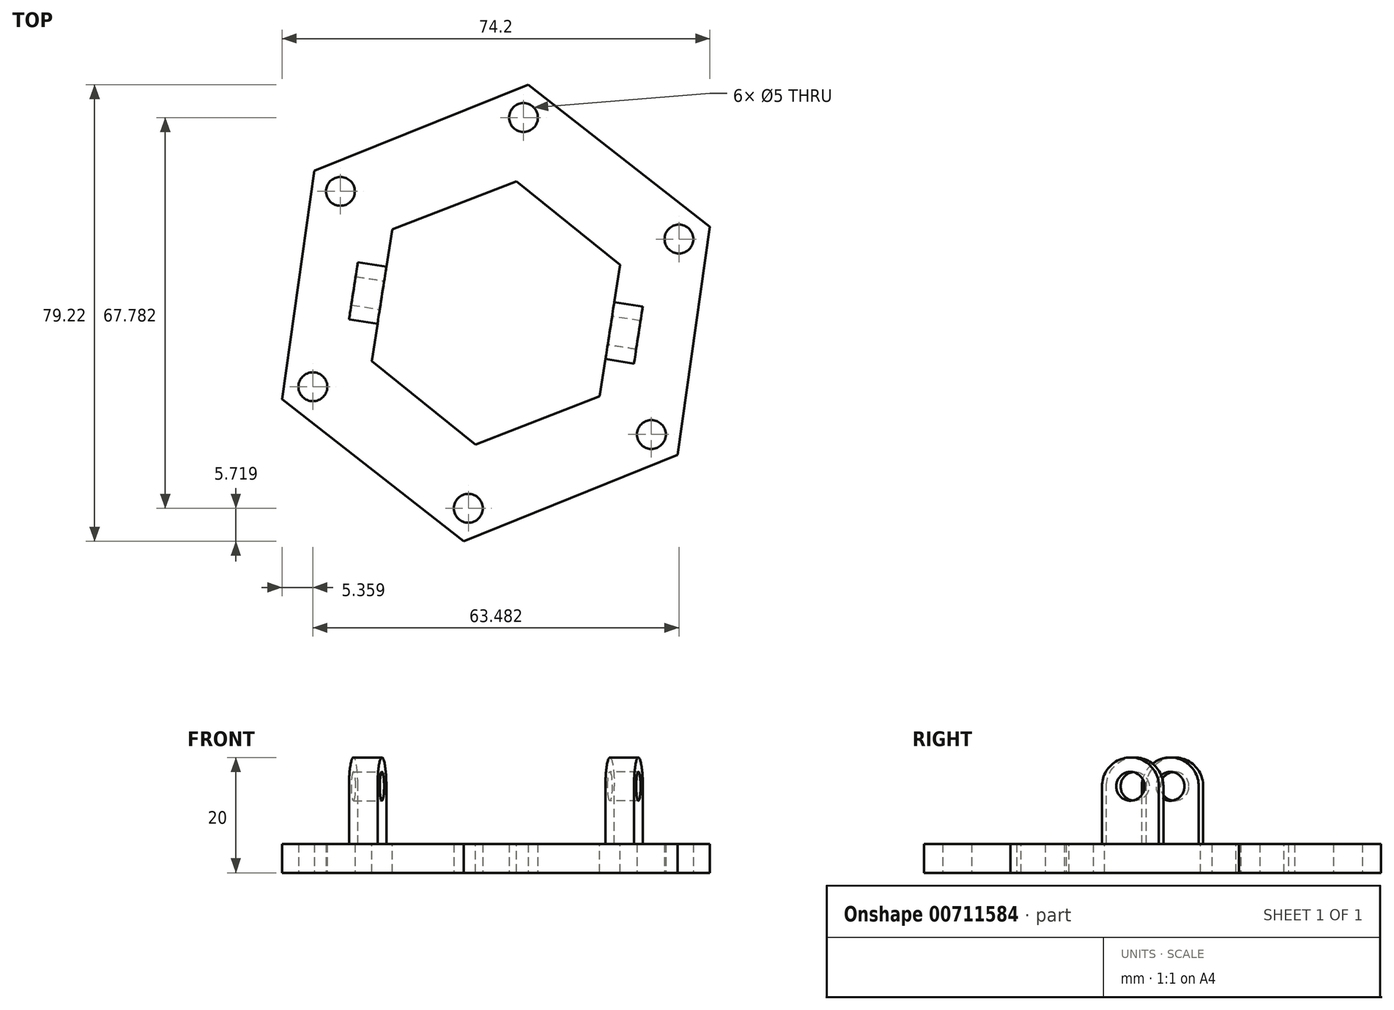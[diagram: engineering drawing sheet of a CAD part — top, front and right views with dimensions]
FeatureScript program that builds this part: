
annotation { "Feature Type Name" : "Feature", "Feature Type Description" : "" }
export const myFeature = defineFeature(function(context is Context, id is Id, definition is map)
    precondition{}
    {
        {
            var Q0;
            Q0=qCreatedBy(makeId("Top.planeOp"),FACE);
            var sketch = newSketch(context, id + "F0", { "sketchPlane" : qUnion([Q0])});
            skCircle(sketch, "E0.cCircle", {"center": v(0, 0) * mm, "radius": 34.64 * mm, "construction": true});
            skLineSegment(sketch, "E0.0", {"start": v(37.1, 14.96) * mm, "end": v(31.5, -24.64) * mm});
            skLineSegment(sketch, "E0.1", {"start": v(31.5, -24.64) * mm, "end": v(-5.59, -39.6) * mm});
            skLineSegment(sketch, "E0.2", {"start": v(-5.59, -39.6) * mm, "end": v(-37.1, -14.96) * mm});
            skLineSegment(sketch, "E0.3", {"start": v(-37.1, -14.96) * mm, "end": v(-31.5, 24.64) * mm});
            skLineSegment(sketch, "E0.4", {"start": v(-31.5, 24.64) * mm, "end": v(5.59, 39.6) * mm});
            skLineSegment(sketch, "E0.5", {"start": v(5.59, 39.6) * mm, "end": v(37.1, 14.96) * mm});
            skPoint(sketch, "E0.0.midPoint", {"position": v(34.3, -4.84) * mm});
            skSolve(sketch);
        }
        {
            var Q0;
            Q0=makeQuery(id+"F0.imprint","IMPRINT",FACE,{"disambiguationData":[TD([[makeQuery(id+"F0.imprint","IMPRINT",EDGE,{"derivedFrom":sQuery(id+"F0.wireOp",EDGE,"E0.0")}),-1.0]])]});
            extrude(context, id + "F1", {"entities" : qUnion([Q0]), "depth" : 5 * mm, "offsetDistance" : 25 * mm});
        }
        {
            var Q0;
            Q0=makeQuery(id+"F1.opExtrude","CAP_FACE",FACE,{"disambiguationData":[OSD([sQuery(id+"F0.wireOp",EDGE,"E0.0"),sQuery(id+"F0.wireOp",EDGE,"E0.1"),sQuery(id+"F0.wireOp",EDGE,"E0.2"),sQuery(id+"F0.wireOp",EDGE,"E0.3"),sQuery(id+"F0.wireOp",EDGE,"E0.4"),sQuery(id+"F0.wireOp",EDGE,"E0.5")])],"isStart":true});
            var sketch = newSketch(context, id + "F2", { "sketchPlane" : qUnion([Q0])});
            skCircle(sketch, "E1", {"center": v(26.96, 21.09) * mm, "radius": 2.5 * mm});
            skCircle(sketch, "E2", {"center": v(-4.78, 33.9) * mm, "radius": 2.5 * mm});
            skCircle(sketch, "E3", {"center": v(31.74, -12.8) * mm, "radius": 2.5 * mm});
            skCircle(sketch, "E4", {"center": v(4.78, -33.9) * mm, "radius": 2.5 * mm});
            skCircle(sketch, "E5", {"center": v(-26.96, -21.09) * mm, "radius": 2.5 * mm});
            skCircle(sketch, "E6", {"center": v(-31.74, 12.8) * mm, "radius": 2.5 * mm});
            skSolve(sketch);
        }
        {
            var Q0;
            Q0=makeQuery(id+"F2.imprint","IMPRINT",FACE,{"disambiguationData":[TD([[makeQuery(id+"F2.imprint","IMPRINT",EDGE,{"derivedFrom":sQuery(id+"F2.wireOp",EDGE,"E3")}),1.0]])]});
            var Q1;
            Q1=makeQuery(id+"F2.imprint","IMPRINT",FACE,{"disambiguationData":[TD([[makeQuery(id+"F2.imprint","IMPRINT",EDGE,{"derivedFrom":sQuery(id+"F2.wireOp",EDGE,"E4")}),1.0]])]});
            var Q2;
            Q2=makeQuery(id+"F2.imprint","IMPRINT",FACE,{"disambiguationData":[TD([[makeQuery(id+"F2.imprint","IMPRINT",EDGE,{"derivedFrom":sQuery(id+"F2.wireOp",EDGE,"E5")}),1.0]])]});
            var Q3;
            Q3=makeQuery(id+"F2.imprint","IMPRINT",FACE,{"disambiguationData":[TD([[makeQuery(id+"F2.imprint","IMPRINT",EDGE,{"derivedFrom":sQuery(id+"F2.wireOp",EDGE,"E6")}),1.0]])]});
            var Q4;
            Q4=makeQuery(id+"F2.imprint","IMPRINT",FACE,{"disambiguationData":[TD([[makeQuery(id+"F2.imprint","IMPRINT",EDGE,{"derivedFrom":sQuery(id+"F2.wireOp",EDGE,"E2")}),1.0]])]});
            var Q5;
            Q5=makeQuery(id+"F2.imprint","IMPRINT",FACE,{"disambiguationData":[TD([[makeQuery(id+"F2.imprint","IMPRINT",EDGE,{"derivedFrom":sQuery(id+"F2.wireOp",EDGE,"E1")}),1.0]])]});
            extrude(context, id + "F3", {"entities" : qUnion([Q0, Q1, Q2, Q3, Q4, Q5]), "operationType" : NewBodyOperationType.REMOVE, "oppositeDirection" : true, "depth" : 25 * mm, "offsetDistance" : 25 * mm});
        }
        {
            var Q0;
            Q0=makeQuery(id+"F1.opExtrude","CAP_FACE",FACE,{"disambiguationData":[OSD([sQuery(id+"F0.wireOp",EDGE,"E0.0"),sQuery(id+"F0.wireOp",EDGE,"E0.1"),sQuery(id+"F0.wireOp",EDGE,"E0.2"),sQuery(id+"F0.wireOp",EDGE,"E0.3"),sQuery(id+"F0.wireOp",EDGE,"E0.4"),sQuery(id+"F0.wireOp",EDGE,"E0.5")])],"isStart":false});
            var sketch = newSketch(context, id + "F4", { "sketchPlane" : qUnion([Q0])});
            skCircle(sketch, "E7.cCircle", {"center": v(0, 0) * mm, "radius": 20 * mm, "construction": true});
            skLineSegment(sketch, "E7.0", {"start": v(21.53, 8.34) * mm, "end": v(18, -14.48) * mm});
            skLineSegment(sketch, "E7.1", {"start": v(18, -14.48) * mm, "end": v(-3.54, -22.82) * mm});
            skLineSegment(sketch, "E7.2", {"start": v(-3.54, -22.82) * mm, "end": v(-21.53, -8.34) * mm});
            skLineSegment(sketch, "E7.3", {"start": v(-21.53, -8.34) * mm, "end": v(-18, 14.48) * mm});
            skLineSegment(sketch, "E7.4", {"start": v(-18, 14.48) * mm, "end": v(3.54, 22.82) * mm});
            skLineSegment(sketch, "E7.5", {"start": v(3.54, 22.82) * mm, "end": v(21.53, 8.34) * mm});
            skPoint(sketch, "E7.0.midPoint", {"position": v(19.76, -3.07) * mm});
            skSolve(sketch);
        }
        {
            var Q0;
            Q0=makeQuery(id+"F4.imprint","IMPRINT",FACE,{"disambiguationData":[TD([[makeQuery(id+"F4.imprint","IMPRINT",EDGE,{"derivedFrom":sQuery(id+"F4.wireOp",EDGE,"E7.0")}),-1.0]])]});
            extrude(context, id + "F5", {"entities" : qUnion([Q0]), "operationType" : NewBodyOperationType.REMOVE, "oppositeDirection" : true, "depth" : 6 * mm, "offsetDistance" : 25 * mm});
        }
        {
            var Q0;
            Q0=makeQuery(id+"F5.boolean.opBoolean","COPY",FACE,{"derivedFrom":makeQuery(id+"F5.opExtrude","SWEPT_FACE",FACE,{"disambiguationData":[OSD([sQuery(id+"F4.wireOp",EDGE,"E7.3")])]})});
            var sketch = newSketch(context, id + "F6", { "sketchPlane" : qUnion([Q0])});
            skLineSegment(sketch, "E8", {"start": v(-5, 5) * mm, "end": v(-5, 15) * mm});
            skLineSegment(sketch, "E9", {"start": v(5, 5) * mm, "end": v(5, 15) * mm});
            skArc(sketch, "E10", {"start": v(5, 15) * mm, "mid": v(0, 20) * mm, "end": v(-5, 15) * mm});
            skSolve(sketch);
        }
        {
            var Q0;
            {var subQ0=sQuery(id+"F6.wireOp",EDGE,"E8");Q0=makeQuery(id+"F6.imprint","IMPRINT",FACE,{"disambiguationData":[TD([[makeQuery(id+"F6.imprint","IMPRINT",EDGE,{"derivedFrom":subQ0}),-1.0]])]});}
            extrude(context, id + "F7", {"entities" : qUnion([Q0]), "operationType" : NewBodyOperationType.ADD, "oppositeDirection" : true, "depth" : 5 * mm, "offsetDistance" : 25 * mm});
        }
        {
            var Q0;
            {var subQ0=sQuery(id+"F4.wireOp",EDGE,"E7.3");Q0=makeQuery(id+"F7.boolean.opBoolean","MERGE",FACE,{"derivedFrom":[makeQuery(id+"F5.boolean.opBoolean","COPY",FACE,{"derivedFrom":makeQuery(id+"F5.opExtrude","SWEPT_FACE",FACE,{"disambiguationData":[OSD([subQ0])]})}),makeQuery(id+"F7.opExtrude","CAP_FACE",FACE,{"disambiguationData":[OSD([subQ0,sQuery(id+"F6.wireOp",EDGE,"E8"),sQuery(id+"F6.wireOp",EDGE,"E9"),sQuery(id+"F6.wireOp",EDGE,"E10")])],"isStart":true})]});}
            var sketch = newSketch(context, id + "F8", { "sketchPlane" : qUnion([Q0])});
            skCircle(sketch, "E11", {"center": v(0, 15) * mm, "radius": 2.5 * mm});
            skSolve(sketch);
        }
        {
            var Q0;
            Q0=makeQuery(id+"F8.imprint","IMPRINT",FACE,{"disambiguationData":[TD([[makeQuery(id+"F8.imprint","IMPRINT",EDGE,{"derivedFrom":sQuery(id+"F8.wireOp",EDGE,"E11")}),1.0]])]});
            extrude(context, id + "F9", {"entities" : qUnion([Q0]), "operationType" : NewBodyOperationType.REMOVE, "oppositeDirection" : true, "depth" : 25 * mm, "offsetDistance" : 25 * mm});
        }
        {
            var Q0;
            Q0=makeQuery(id+"F5.boolean.opBoolean","COPY",FACE,{"derivedFrom":makeQuery(id+"F5.opExtrude","SWEPT_FACE",FACE,{"disambiguationData":[OSD([sQuery(id+"F4.wireOp",EDGE,"E7.0")])]})});
            var sketch = newSketch(context, id + "F10", { "sketchPlane" : qUnion([Q0])});
            skLineSegment(sketch, "E12", {"start": v(-5, 5) * mm, "end": v(-5, 15) * mm});
            skLineSegment(sketch, "E13", {"start": v(5, 5) * mm, "end": v(5, 15) * mm});
            skArc(sketch, "E14", {"start": v(5, 15) * mm, "mid": v(0, 20) * mm, "end": v(-5, 15) * mm});
            skCircle(sketch, "E15", {"center": v(0, 15) * mm, "radius": 2.5 * mm});
            skSolve(sketch);
        }
        {
            var Q0;
            {var subQ1=sQuery(id+"F10.wireOp",EDGE,"E12");Q0=makeQuery(id+"F10.imprint","IMPRINT",FACE,{"disambiguationData":[TD([[makeQuery(id+"F10.imprint","IMPRINT",EDGE,{"derivedFrom":subQ1}),-1.0]])]});}
            extrude(context, id + "F11", {"entities" : qUnion([Q0]), "operationType" : NewBodyOperationType.ADD, "oppositeDirection" : true, "depth" : 5 * mm, "offsetDistance" : 25 * mm});
        }
    });
